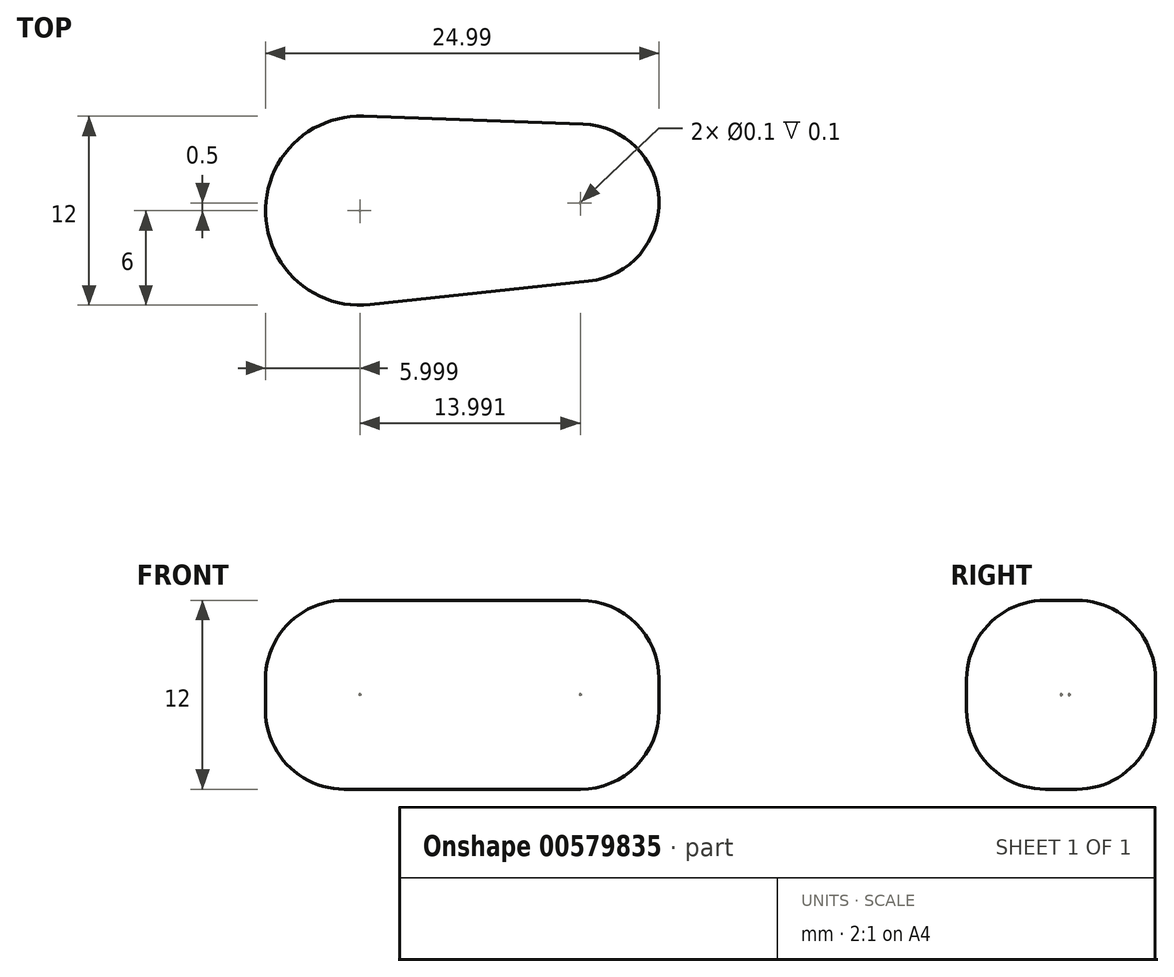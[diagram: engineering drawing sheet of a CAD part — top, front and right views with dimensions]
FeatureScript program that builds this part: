
annotation { "Feature Type Name" : "Feature", "Feature Type Description" : "" }
export const myFeature = defineFeature(function(context is Context, id is Id, definition is map)
    precondition{}
    {
        {
            assignVariable(context, id + "F0", {"variableType" : VariableType.LENGTH, "name" : "l", "lengthValue" : 1 * mm});
        }
        {
            var Q0;
            Q0=qCreatedBy(makeId("Top.planeOp"),FACE);
            var sketch = newSketch(context, id + "F1", { "sketchPlane" : qUnion([Q0])});
            skCircle(sketch, "E0", {"center": v(-19, -6) * mm, "radius": 6 * mm});
            skCircle(sketch, "E1", {"center": v(-5, -5.5) * mm, "radius": 5 * mm});
            skLineSegment(sketch, "E2", {"start": v(-18.78, 0) * mm, "end": v(-4.82, -0.5) * mm});
            skLineSegment(sketch, "E3", {"start": v(-18.35, -11.97) * mm, "end": v(-4.46, -10.47) * mm});
            skLineSegment(sketch, "E4", {"start": v(0, 0) * mm, "end": v(0, -15.4) * mm, "construction": true});
            skLineSegment(sketch, "E5", {"start": v(0.64, 0) * mm, "end": v(-33.48, 0) * mm, "construction": true});
            skCircle(sketch, "E6", {"center": v(-19, -6) * mm, "radius": 0.05 * mm});
            skCircle(sketch, "E7", {"center": v(-5, -5.5) * mm, "radius": 0.05 * mm});
            skSolve(sketch);
        }
        {
            var Q0;
            Q0=qSketchRegion(id+"F1",true);
            var Q1;
            Q1=makeQuery(id+"F1.imprint","IMPRINT",FACE,{"disambiguationData":[TD([[makeQuery(id+"F1.imprint","IMPRINT",EDGE,{"derivedFrom":sQuery(id+"F1.wireOp",EDGE,"6d6239f2-36b7-4a5e-b3e6-5e9e5222fc7c")}),1.0]])]});
            var Q2;
            Q2=makeQuery(id+"F1.imprint","IMPRINT",FACE,{"disambiguationData":[TD([[makeQuery(id+"F1.imprint","IMPRINT",EDGE,{"derivedFrom":sQuery(id+"F1.wireOp",EDGE,"2646e586-5577-401d-ae3b-539c4553b434")}),1.0]])]});
            var Q3;
            Q3=makeQuery(id+"F1.imprint","IMPRINT",FACE,{"disambiguationData":[TD([[makeQuery(id+"F1.imprint","IMPRINT",EDGE,{"derivedFrom":sQuery(id+"F1.wireOp",EDGE,"pNU19z77-JYq1-BsRa-hIak-k1DsLWVGxT2d")}),1.0]])]});
            var Q4;
            Q4=makeQuery(id+"F1.imprint","IMPRINT",FACE,{"disambiguationData":[TD([[makeQuery(id+"F1.imprint","IMPRINT",EDGE,{"derivedFrom":sQuery(id+"F1.wireOp",EDGE,"2J5k5qBS-T8st-Zxik-poDU-rb25eGofRYkS")}),1.0]])]});
            var Q5;
            Q5=makeQuery(id+"F1.imprint","IMPRINT",FACE,{"disambiguationData":[TD([[makeQuery(id+"F1.imprint","IMPRINT",EDGE,{"derivedFrom":sQuery(id+"F1.wireOp",EDGE,"E6")}),1.0]])]});
            var Q6;
            Q6=makeQuery(id+"F1.imprint","IMPRINT",FACE,{"disambiguationData":[TD([[makeQuery(id+"F1.imprint","IMPRINT",EDGE,{"derivedFrom":sQuery(id+"F1.wireOp",EDGE,"E7")}),1.0]])]});
            extrude(context, id + "F2", {"entities" : qUnion([Q0, Q1, Q2, Q3, Q4, Q5, Q6]), "depth" : 12 * getVariable(context, 'l'), "offsetDistance" : 25 * mm, "symmetric" : true});
        }
        {
            var Q0;
            Q0=makeQuery(id+"F1.imprint","IMPRINT",FACE,{"disambiguationData":[TD([[makeQuery(id+"F1.imprint","IMPRINT",EDGE,{"derivedFrom":sQuery(id+"F1.wireOp",EDGE,"E6")}),1.0]])]});
            var Q1;
            Q1=makeQuery(id+"F1.imprint","IMPRINT",FACE,{"disambiguationData":[TD([[makeQuery(id+"F1.imprint","IMPRINT",EDGE,{"derivedFrom":sQuery(id+"F1.wireOp",EDGE,"E7")}),1.0]])]});
            extrude(context, id + "F3", {"entities" : qUnion([Q0, Q1]), "operationType" : NewBodyOperationType.REMOVE, "depth" : 0.1 * mm, "offsetDistance" : 25 * mm, "symmetric" : true});
        }
        {
            var Q0;
            Q0=makeQuery(id+"F2.opExtrude","CAP_FACE",FACE,{"disambiguationData":[OSD([sQuery(id+"F1.wireOp",EDGE,"E0"),sQuery(id+"F1.wireOp",EDGE,"E1"),sQuery(id+"F1.wireOp",EDGE,"E2"),sQuery(id+"F1.wireOp",EDGE,"E3")])],"isStart":false});
            var Q1;
            Q1=makeQuery(id+"F2.opExtrude","CAP_FACE",FACE,{"disambiguationData":[OSD([sQuery(id+"F1.wireOp",EDGE,"E0"),sQuery(id+"F1.wireOp",EDGE,"E1"),sQuery(id+"F1.wireOp",EDGE,"E2"),sQuery(id+"F1.wireOp",EDGE,"E3")])],"isStart":true});
            fillet(context, id + "F4", {"entities" : qUnion([Q0, Q1]), "radius" : 5 * getVariable(context, 'l'), "tangentPropagation" : true, "allowEdgeOverflow" : false});
        }
    });
